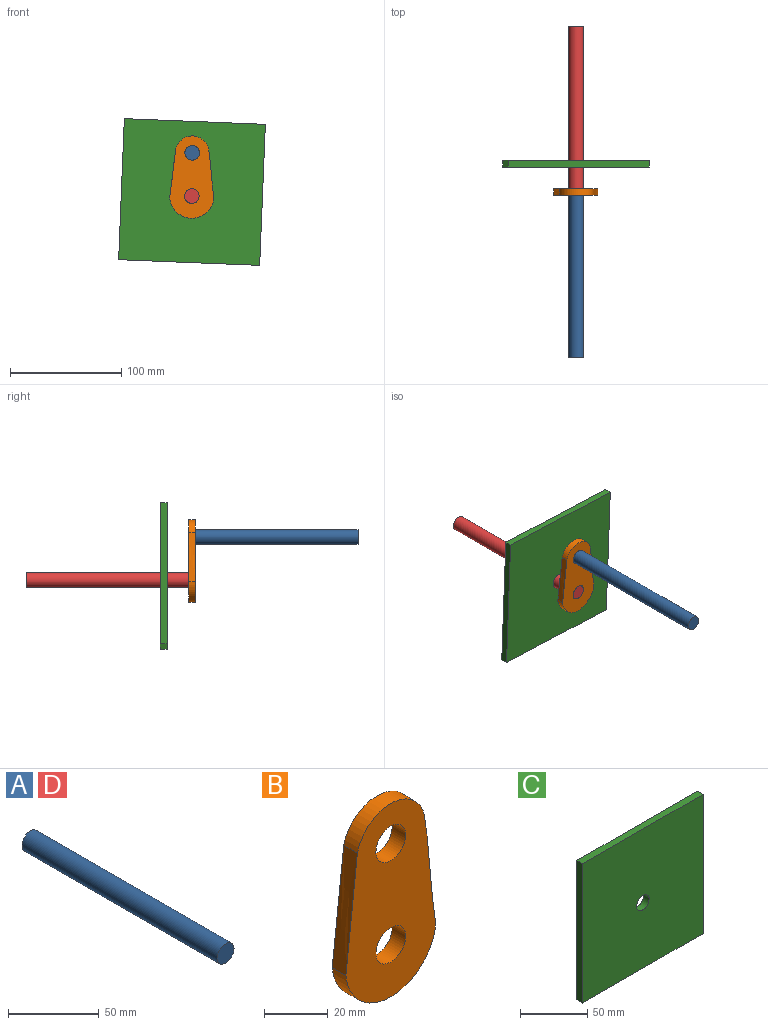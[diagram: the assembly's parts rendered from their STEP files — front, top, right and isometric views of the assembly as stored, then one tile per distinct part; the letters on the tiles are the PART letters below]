
ASSEMBLY  parts=4 mates=3
PART A: 3 faces, bbox 13.1x152.4x13.1 mm
  f0: cylinder r=6.54mm len=152.4mm, axis (0,1,0), area 6262.9mm2, adj f1,f2
  f1: plane 13.08x13.08mm, normal (0,-1,0), area 134.4mm2, adj f0
  f2: plane 13.08x13.08mm, normal (0,1,0), area 134.4mm2, adj f0
PART B: 8 faces, bbox 39.8x6x74.1 mm
  f0: extruded ~44.31x6.05mm, area 269.7mm2, adj f1,f5,f6,f7
  f1: cylinder r=15.24mm len=29.62mm, axis (0,1,0), area 245.4mm2, adj f0,f2,f6,f7
  f2: extruded ~44.31x6.05mm, area 269.7mm2, adj f1,f5,f6,f7
  f3: cylinder r=6.6mm len=13.21mm, axis (0,1,0), area 250.8mm2, adj f6,f7
  f4: cylinder r=6.6mm len=13.21mm, axis (0,1,0), area 250.8mm2, adj f6,f7
  f5: cylinder r=19.97mm len=39.78mm, axis (0,1,0), area 357.2mm2, adj f0,f2,f6,f7
  f6: plane 74.1x39.78mm, normal (0,-1,0), area 2073.3mm2, adj f0,f1,f2,f3,f4,f5
  f7: plane 74.1x39.78mm, normal (0,1,0), area 2073.3mm2, adj f0,f1,f2,f3,f4,f5
PART C: 7 faces, bbox 127x6x127 mm
  f0: plane 127x6.05mm, normal (0,0,1), area 767.7mm2, adj f1,f4,f5,f6
  f1: plane 127x6.05mm, normal (-1,0,0), area 767.7mm2, adj f0,f2,f5,f6
  f2: plane 127x6.05mm, normal (0,0,-1), area 767.7mm2, adj f1,f4,f5,f6
  f3: cylinder r=6.6mm len=13.21mm, axis (0,1,0), area 250.8mm2, adj f5,f6
  f4: plane 127x6.05mm, normal (1,0,0), area 767.7mm2, adj f0,f2,f5,f6
  f5: plane 127x127mm, normal (0,-1,0), area 15992mm2, adj f0,f1,f2,f3,f4
  f6: plane 127x127mm, normal (0,1,0), area 15992mm2, adj f0,f1,f2,f3,f4
PART D: same geometry as A
PLACE A rot(axis=(0,1,0),0.5deg) t=(-104.29,26.24,39.53)mm
PLACE B rot(axis=(0,1,0),0.5deg) t=(-63.17,26.24,40.67)mm
PLACE C rot(axis=(0,1,0),2.3deg) t=(-110.57,51.64,44.72)mm fixed
PLACE D rot(axis=(0,1,0),92.3deg) t=(-151.31,172.6,36.25)mm
MATE fastened C.f3 <-> D.f0  axis (0,-1,0) through (-110.72,45.6,41.06)mm
MATE revolute D.f0 <-> B.f4  axis (0,-1,0) through (-110.72,20.2,41.06)mm
MATE fastened B.f1 <-> A.f0  axis (0,1,0) through (-110.4,26.24,79.94)mm
